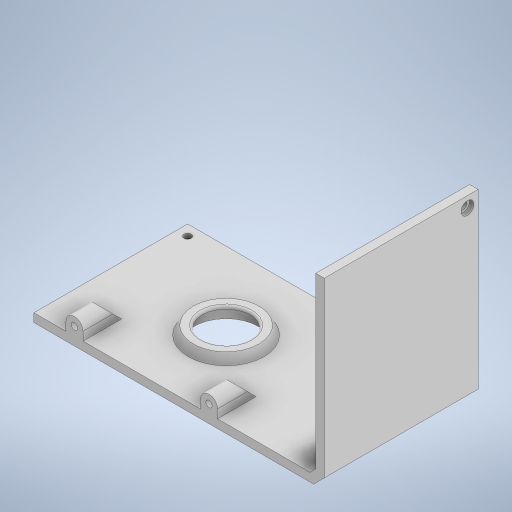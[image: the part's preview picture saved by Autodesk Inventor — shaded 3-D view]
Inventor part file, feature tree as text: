
AUTODESK INVENTOR PART (.ipt)
format: ipt  version: 2023 (Build 270158000, 158)  size: 430,080 bytes
history: native  units: mm
features: sketch x13, extrude x11, fillet x3, projected_geometry x3, other x2, revolve x2, hole x1, chamfer x1
ambient origin geometry x8: Origin, YZ Plane, XZ Plane, XY Plane, X Axis, Y Axis, Z Axis, Center Point
bodies: Body1 (feature_tree)
feature tree (36):
  other  "솔리드1"
  extrude  "돌출1"  Depth=140.0mm
  extrude  "돌출2"  Depth=90.0mm
  hole  "구멍1"  [1 undecoded]
  other  "작업 평면1"
  sketch  "스케치5"
  revolve  "회전1"
  revolve  "회전2"
  fillet  "모깎기1"  Radius=5.0mm
  extrude  "돌출3"  Depth=4.0mm
  extrude  "돌출4"  Depth=72.0mm TaperAngle=0.0deg
  extrude  "돌출5"  Depth=53.0mm
  extrude  "돌출6"  Depth=69.0mm
  extrude  "돌출7"  Depth=80.0mm
  extrude  "돌출8"  Depth=65.0mm
  extrude  "돌출9"  Depth=3.0mm
  extrude  "돌출10"  Depth=30.0mm
  chamfer  "모따기1"  Distance=42.0mm
  extrude  "돌출11"  Depth=6.0mm
  fillet  "모깎기2"  Radius=6.0mm
  fillet  "모깎기3"  Radius=6.0mm
  sketch  "스케치1"
  sketch  "스케치2"
  sketch  "스케치3"
  projected_geometry  "투영된 루프1"
  projected_geometry  "투영된 루프2"
  projected_geometry  "투영된 루프3"
  sketch  "스케치6"
  sketch  "스케치7"
  sketch  "스케치8"
  sketch  "스케치9"
  sketch  "스케치10"
  sketch  "스케치11"
  sketch  "스케치12"
  sketch  "스케치13"
  sketch  "스케치14"
note: 1 required parameter value undecoded (feature->parameter linkage not recoverable at this tier; creation-order binding heuristic only, values carry confidence <= 0.55)
